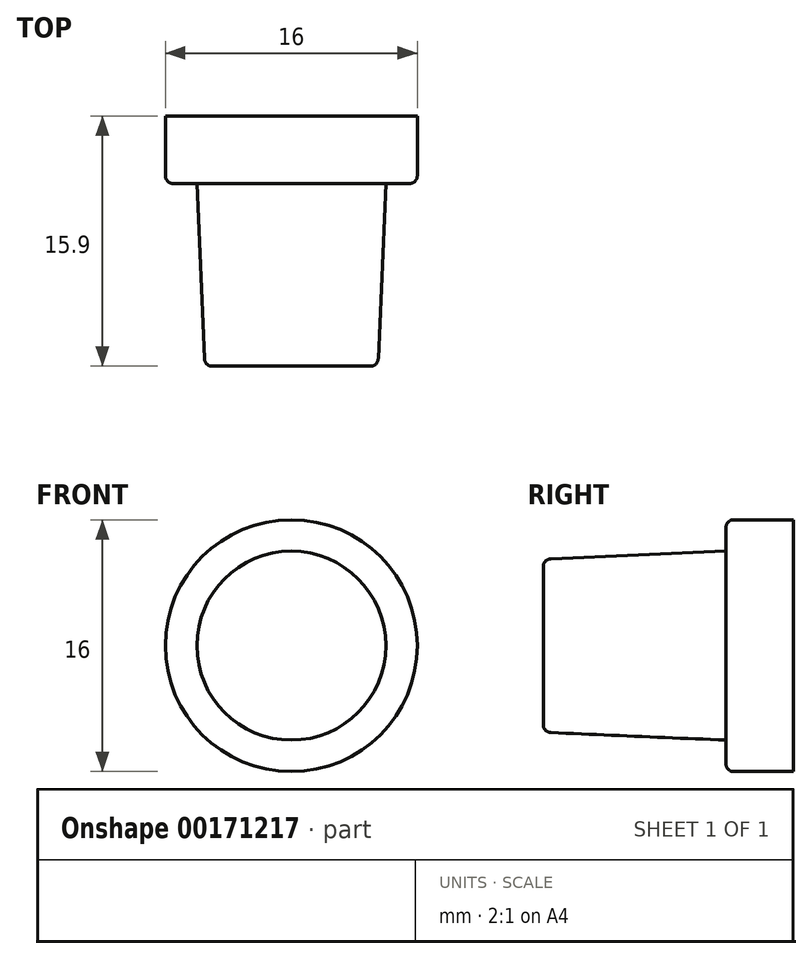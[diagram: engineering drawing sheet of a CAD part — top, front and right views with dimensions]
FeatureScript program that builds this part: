
annotation { "Feature Type Name" : "Feature", "Feature Type Description" : "" }
export const myFeature = defineFeature(function(context is Context, id is Id, definition is map)
    precondition{}
    {
        {
            var Q0;
            Q0=qCreatedBy(makeId("Front.planeOp"),FACE);
            var sketch = newSketch(context, id + "F0", { "sketchPlane" : qUnion([Q0])});
            skCircle(sketch, "E0", {"center": v(0, 0) * mm, "radius": 8 * mm});
            skCircle(sketch, "E1", {"center": v(0, 0) * mm, "radius": 6.75 * mm});
            skCircle(sketch, "E2", {"center": v(0, 0) * mm, "radius": 5.52 * mm});
            skSolve(sketch);
        }
        {
            var Q0;
            Q0=makeQuery(id+"F0.imprint","IMPRINT",FACE,{"disambiguationData":[TD([[makeQuery(id+"F0.imprint","IMPRINT",EDGE,{"derivedFrom":sQuery(id+"F0.wireOp",EDGE,"E0")}),1.0]])]});
            var Q1;
            Q1=makeQuery(id+"F0.imprint","IMPRINT",FACE,{"disambiguationData":[TD([[makeQuery(id+"F0.imprint","IMPRINT",EDGE,{"derivedFrom":sQuery(id+"F0.wireOp",EDGE,"E1")}),1.0]])]});
            var Q2;
            Q2=makeQuery(id+"F0.imprint","IMPRINT",FACE,{"disambiguationData":[TD([[makeQuery(id+"F0.imprint","IMPRINT",EDGE,{"derivedFrom":sQuery(id+"F0.wireOp",EDGE,"E2")}),1.0]])]});
            extrude(context, id + "F1", {"entities" : qUnion([Q0, Q1, Q2]), "depth" : 4.3 * mm});
        }
        {
            var Q0;
            Q0=qCreatedBy(makeId("Right.planeOp"),FACE);
            var sketch = newSketch(context, id + "F2", { "sketchPlane" : qUnion([Q0])});
            skLineSegment(sketch, "E3", {"start": v(0, 0) * mm, "end": v(0, 6) * mm});
            skLineSegment(sketch, "E4", {"start": v(0, 6) * mm, "end": v(-4.3, 6) * mm});
            skLineSegment(sketch, "E5", {"start": v(-4.3, 6) * mm, "end": v(-15.9, 5.5) * mm});
            skLineSegment(sketch, "E6", {"start": v(-15.9, 5.5) * mm, "end": v(-15.9, 0) * mm});
            skLineSegment(sketch, "E7", {"start": v(-15.9, 0) * mm, "end": v(0, 0) * mm});
            skSolve(sketch);
        }
        {
            var Q0;
            Q0=makeQuery(id+"F2.imprint","IMPRINT",FACE,{"disambiguationData":[TD([[makeQuery(id+"F2.imprint","IMPRINT",EDGE,{"derivedFrom":sQuery(id+"F2.wireOp",EDGE,"E3")}),1.0]])]});
            var Q1;
            Q1=sQuery(id+"F2.wireOp",EDGE,"E7");
            revolve(context, id + "F3", {"operationType" : NewBodyOperationType.ADD, "entities" : qUnion([Q0]), "axis" : qUnion([Q1]), "revolveType" : RevolveType.FULL});
        }
        {
            var Q0;
            Q0=makeQuery(id+"F3.opRevolve","SWEPT_EDGE",EDGE,{"disambiguationData":[OSD([sQuery(id+"F2.wireOp",EDGE,"E5"),sQuery(id+"F2.wireOp",EDGE,"E6")])]});
            var Q1;
            Q1=makeQuery(id+"F1.opExtrude","CAP_EDGE",EDGE,{"disambiguationData":[OSD([sQuery(id+"F0.wireOp",EDGE,"E0")])],"isStart":false});
            fillet(context, id + "F4", {"entities" : qUnion([Q0, Q1]), "radius" : .5 * mm, "tangentPropagation" : true, "allowEdgeOverflow" : false});
        }
    });
